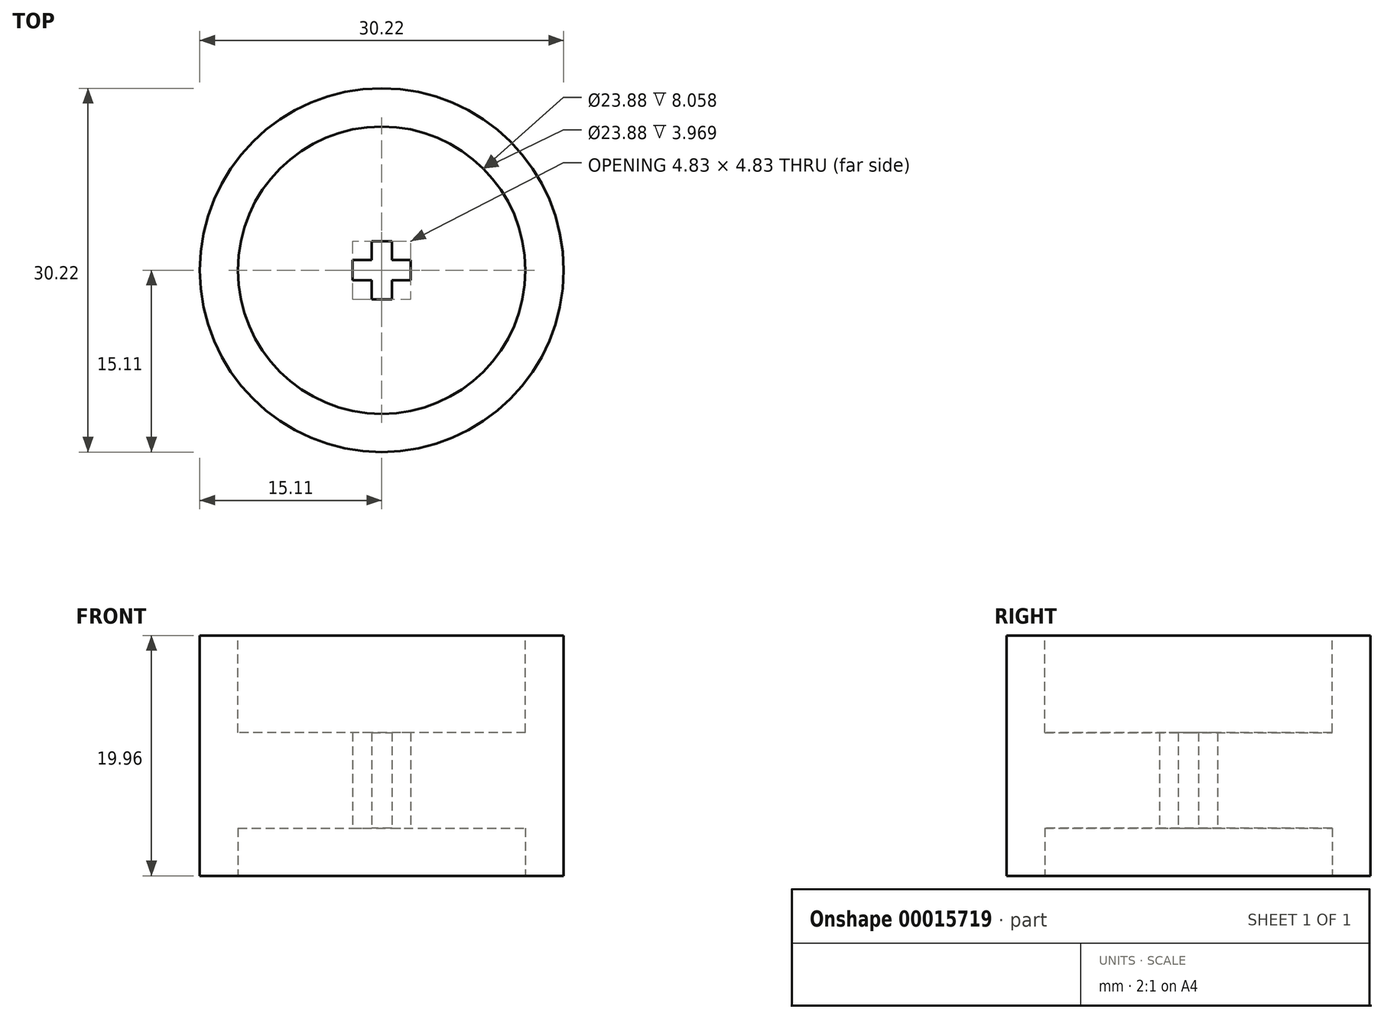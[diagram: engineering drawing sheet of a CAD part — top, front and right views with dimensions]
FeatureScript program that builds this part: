
annotation { "Feature Type Name" : "Feature", "Feature Type Description" : "" }
export const myFeature = defineFeature(function(context is Context, id is Id, definition is map)
    precondition{}
    {
        {
            var Q0;
            Q0=qCreatedBy(makeId("Top.planeOp"),FACE);
            var sketch = newSketch(context, id + "F0", { "sketchPlane" : qUnion([Q0])});
            skCircle(sketch, "E0", {"center": v(0, 0) * mm, "radius": 15.11 * mm});
            skLineSegment(sketch, "E1.rect.bottom", {"start": v(-0.84, 2.41) * mm, "end": v(0.84, 2.41) * mm});
            skLineSegment(sketch, "E1.rect.top", {"start": v(-0.84, -2.41) * mm, "end": v(0.84, -2.41) * mm});
            skLineSegment(sketch, "E1.rect.left", {"start": v(-0.84, 2.41) * mm, "end": v(-0.84, -2.41) * mm});
            skLineSegment(sketch, "E1.rect.right", {"start": v(0.84, 2.41) * mm, "end": v(0.84, -2.41) * mm});
            skLineSegment(sketch, "E2.rect.bottom", {"start": v(2.41, 0.84) * mm, "end": v(-2.41, 0.84) * mm});
            skLineSegment(sketch, "E2.rect.top", {"start": v(2.41, -0.84) * mm, "end": v(-2.41, -0.84) * mm});
            skLineSegment(sketch, "E2.rect.left", {"start": v(2.41, 0.84) * mm, "end": v(2.41, -0.84) * mm});
            skLineSegment(sketch, "E2.rect.right", {"start": v(-2.41, 0.84) * mm, "end": v(-2.41, -0.84) * mm});
            skSolve(sketch);
        }
        {
            var Q0;
            Q0=qSketchRegion(id+"F0",true);
            extrude(context, id + "F1", {"entities" : qUnion([Q0]), "depth" : 19.96 * mm});
        }
        {
            var Q0;
            Q0=makeQuery(id+"F1.opExtrude","CAP_FACE",FACE,{"disambiguationData":[OSD([sQuery(id+"F0.wireOp",EDGE,"E0"),sQuery(id+"F0.wireOp",EDGE,"E1.rect.bottom"),sQuery(id+"F0.wireOp",EDGE,"E1.rect.top"),sQuery(id+"F0.wireOp",EDGE,"E1.rect.left"),sQuery(id+"F0.wireOp",EDGE,"E1.rect.right"),sQuery(id+"F0.wireOp",EDGE,"E2.rect.bottom"),sQuery(id+"F0.wireOp",EDGE,"E2.rect.top"),sQuery(id+"F0.wireOp",EDGE,"E2.rect.left"),sQuery(id+"F0.wireOp",EDGE,"E2.rect.right")])],"isStart":false});
            var sketch = newSketch(context, id + "F2", { "sketchPlane" : qUnion([Q0])});
            skCircle(sketch, "E3", {"center": v(0, 0) * mm, "radius": 11.94 * mm});
            skSolve(sketch);
        }
        {
            var Q0;
            Q0=qSketchRegion(id+"F2",true);
            extrude(context, id + "F3", {"entities" : qUnion([Q0]), "operationType" : NewBodyOperationType.REMOVE, "oppositeDirection" : true, "depth" : 8.06 * mm});
        }
        {
            var Q0;
            Q0=makeQuery(id+"F1.opExtrude","CAP_FACE",FACE,{"disambiguationData":[OSD([sQuery(id+"F0.wireOp",EDGE,"E0"),sQuery(id+"F0.wireOp",EDGE,"E1.rect.bottom"),sQuery(id+"F0.wireOp",EDGE,"E1.rect.top"),sQuery(id+"F0.wireOp",EDGE,"E1.rect.left"),sQuery(id+"F0.wireOp",EDGE,"E1.rect.right"),sQuery(id+"F0.wireOp",EDGE,"E2.rect.bottom"),sQuery(id+"F0.wireOp",EDGE,"E2.rect.top"),sQuery(id+"F0.wireOp",EDGE,"E2.rect.left"),sQuery(id+"F0.wireOp",EDGE,"E2.rect.right")])],"isStart":true});
            var sketch = newSketch(context, id + "F4", { "sketchPlane" : qUnion([Q0])});
            skCircle(sketch, "E4", {"center": v(0, 0) * mm, "radius": 11.94 * mm});
            skSolve(sketch);
        }
        {
            var Q0;
            Q0=qSketchRegion(id+"F4",true);
            extrude(context, id + "F5", {"entities" : qUnion([Q0]), "operationType" : NewBodyOperationType.REMOVE, "oppositeDirection" : true, "depth" : 3.97 * mm});
        }
    });
